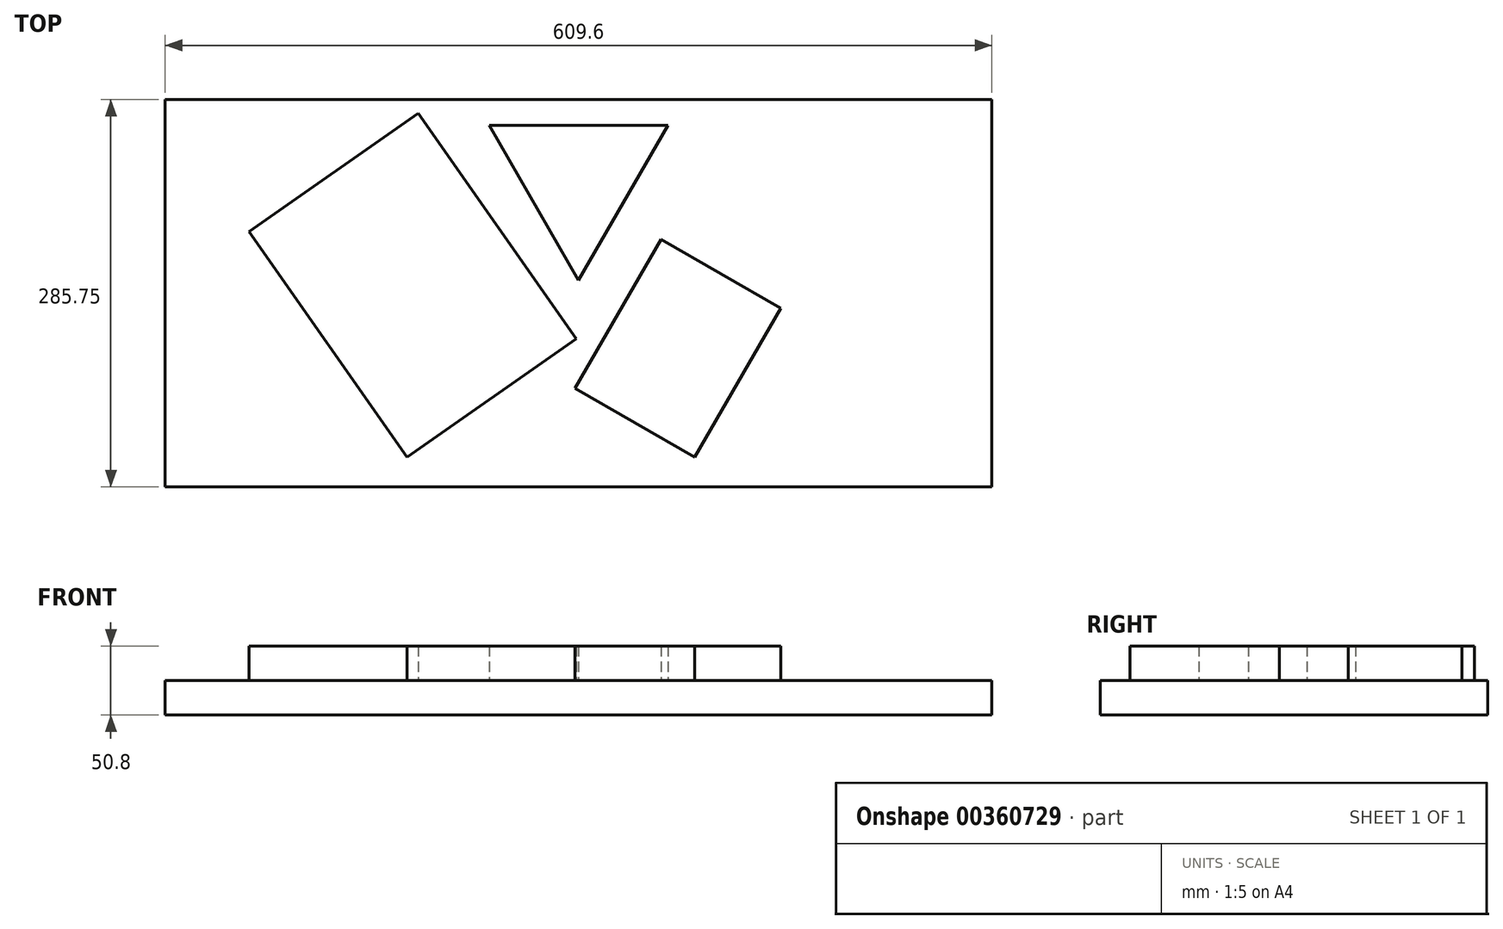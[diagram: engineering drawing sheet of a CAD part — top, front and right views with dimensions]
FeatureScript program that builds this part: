
annotation { "Feature Type Name" : "Feature", "Feature Type Description" : "" }
export const myFeature = defineFeature(function(context is Context, id is Id, definition is map)
    precondition{}
    {
        {
            var Q0;
            Q0=qCreatedBy(makeId("Top.planeOp"),FACE);
            var sketch = newSketch(context, id + "F0", { "sketchPlane" : qUnion([Q0])});
            skLineSegment(sketch, "E0.bottom", {"start": v(304.8, 228.6) * mm, "end": v(-304.8, 228.6) * mm});
            skLineSegment(sketch, "E0.top", {"start": v(304.8, -228.6) * mm, "end": v(-304.8, -228.6) * mm});
            skLineSegment(sketch, "E0.left", {"start": v(304.8, 228.6) * mm, "end": v(304.8, -228.6) * mm});
            skLineSegment(sketch, "E0.right", {"start": v(-304.8, 228.6) * mm, "end": v(-304.8, -228.6) * mm});
            skPoint(sketch, "E0.middle", {"position": v(0, 0) * mm});
            skSolve(sketch);
        }
        {
            var Q0;
            Q0 = qSketchRegion(id + "F0", true);
            extrude(context, id + "F1", {"entities" : qUnion([Q0]), "depth" : 25.4 * mm});
        }
        {
            var Q0;
            Q0=makeQuery(id+"F1.opExtrude","CAP_FACE",FACE,{"disambiguationData":[OSD([sQuery(id+"F0.wireOp",EDGE,"E0.bottom"),sQuery(id+"F0.wireOp",EDGE,"E0.top"),sQuery(id+"F0.wireOp",EDGE,"E0.left"),sQuery(id+"F0.wireOp",EDGE,"E0.right")])],"isStart":false});
            var sketch = newSketch(context, id + "F2", { "sketchPlane" : qUnion([Q0])});
            skCircle(sketch, "E1.cCircle", {"center": v(0, 0) * mm, "radius": 38.1 * mm, "construction": true});
            skLineSegment(sketch, "E1.0", {"start": v(66, 38.1) * mm, "end": v(0, -76.2) * mm});
            skLineSegment(sketch, "E1.1", {"start": v(0, -76.2) * mm, "end": v(-66, 38.1) * mm});
            skLineSegment(sketch, "E1.2", {"start": v(-66, 38.1) * mm, "end": v(66, 38.1) * mm});
            skLineSegment(sketch, "E2.bottom", {"start": v(-242.99, -40.33) * mm, "end": v(-126.43, -206.78) * mm});
            skLineSegment(sketch, "E2.top", {"start": v(-118.15, 47.08) * mm, "end": v(-1.6, -119.37) * mm});
            skLineSegment(sketch, "E2.left", {"start": v(-242.99, -40.33) * mm, "end": v(-118.15, 47.08) * mm});
            skLineSegment(sketch, "E2.right", {"start": v(-126.43, -206.78) * mm, "end": v(-1.6, -119.37) * mm});
            skLineSegment(sketch, "E3.bottom", {"start": v(85.43, -206.78) * mm, "end": v(148.93, -96.8) * mm});
            skLineSegment(sketch, "E3.top", {"start": v(-2.55, -155.98) * mm, "end": v(60.95, -46) * mm});
            skLineSegment(sketch, "E3.left", {"start": v(85.43, -206.78) * mm, "end": v(-2.55, -155.98) * mm});
            skLineSegment(sketch, "E3.right", {"start": v(148.93, -96.8) * mm, "end": v(60.95, -46) * mm});
            skPoint(sketch, "E4", {"position": v(29.2, -100.99) * mm});
            skPoint(sketch, "E5", {"position": v(117.18, -151.79) * mm});
            skPoint(sketch, "E6", {"position": v(104.94, -71.4) * mm});
            skPoint(sketch, "E7", {"position": v(73.2, -126.39) * mm});
            skPoint(sketch, "E8", {"position": v(-59.87, -36.14) * mm});
            skPoint(sketch, "E9", {"position": v(-64.01, -163.07) * mm});
            skPoint(sketch, "E10", {"position": v(-184.7, -123.55) * mm});
            skPoint(sketch, "E11", {"position": v(-122.3, -79.85) * mm});
            skSolve(sketch);
        }
        {
            var Q0;
            Q0 = qSketchRegion(id + "F2", true);
            extrude(context, id + "F3", {"entities" : qUnion([Q0]), "depth" : 25.4 * mm});
        }
        {
            var Q0;
            Q0=makeQuery(id+"F1.opExtrude","SWEPT_FACE",FACE,{"disambiguationData":[OSD([sQuery(id+"F0.wireOp",EDGE,"E0.left")])]});
            var sketch = newSketch(context, id + "F4", { "sketchPlane" : qUnion([Q0])});
            skLineSegment(sketch, "E12.bottom", {"start": v(228.6, 0) * mm, "end": v(57.15, 0) * mm});
            skLineSegment(sketch, "E12.top", {"start": v(228.6, 25.4) * mm, "end": v(57.15, 25.4) * mm});
            skLineSegment(sketch, "E12.left", {"start": v(228.6, 0) * mm, "end": v(228.6, 25.4) * mm});
            skLineSegment(sketch, "E12.right", {"start": v(57.15, 0) * mm, "end": v(57.15, 25.4) * mm});
            skSolve(sketch);
        }
        {
            var Q0;
            Q0 = qSketchRegion(id + "F4", true);
            extrude(context, id + "F5", {"entities" : qUnion([Q0]), "operationType" : NewBodyOperationType.REMOVE, "endBound" : BoundingType.THROUGH_ALL, "oppositeDirection" : true, "depth" : 25.4 * mm});
        }
    });
